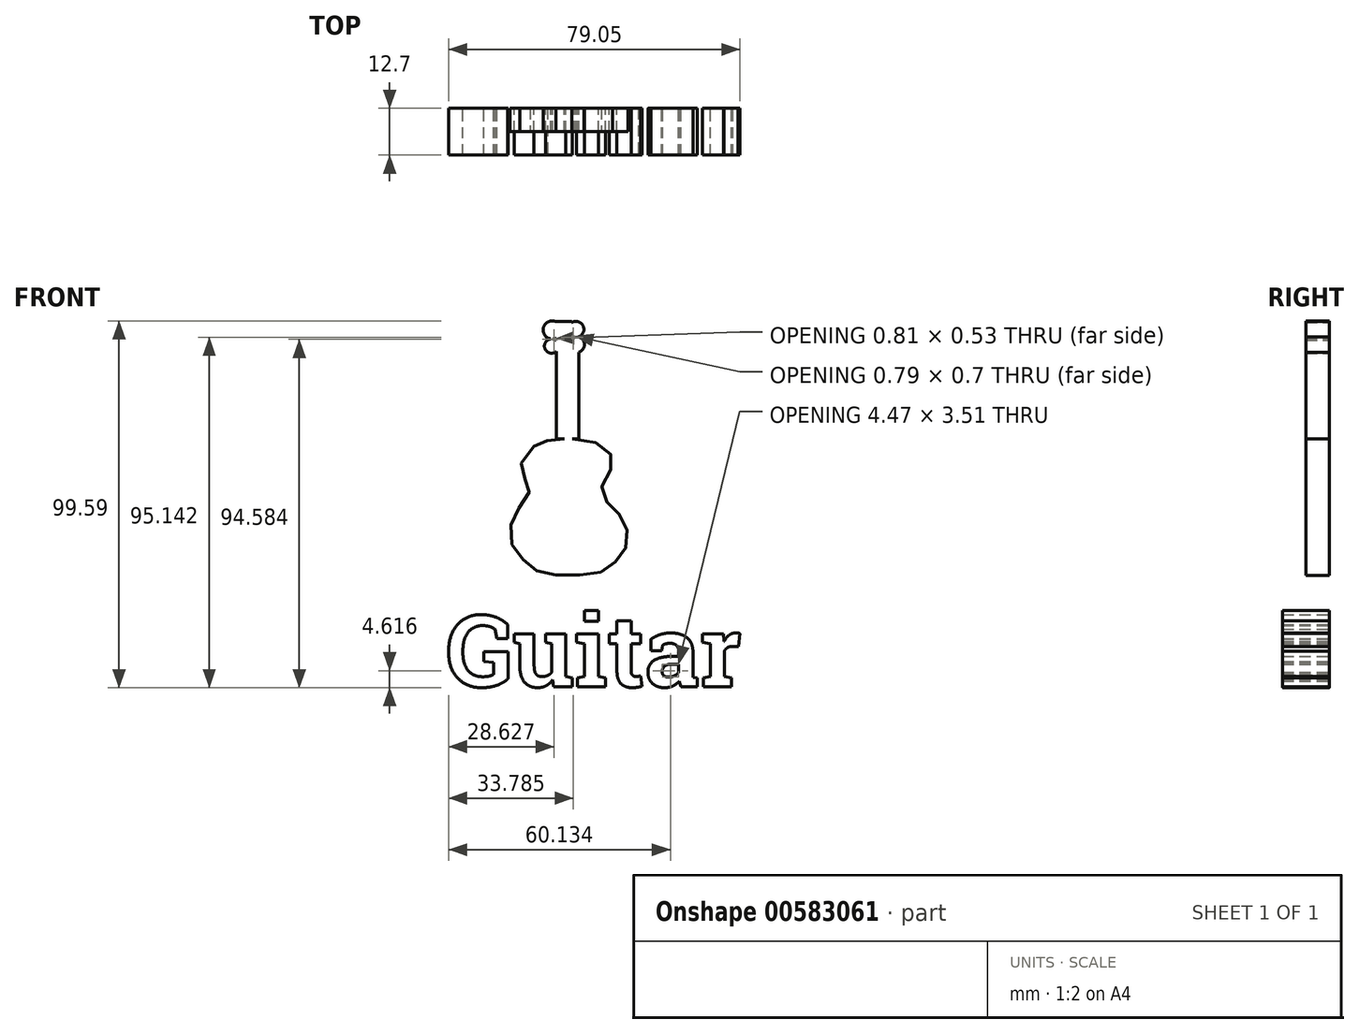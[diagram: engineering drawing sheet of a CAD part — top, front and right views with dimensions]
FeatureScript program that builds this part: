
annotation { "Feature Type Name" : "Feature", "Feature Type Description" : "" }
export const myFeature = defineFeature(function(context is Context, id is Id, definition is map)
    precondition{}
    {
        {
            var Q0;
            Q0=qCreatedBy(makeId("Front.planeOp"),FACE);
            var sketch = newSketch(context, id + "F0", { "sketchPlane" : qUnion([Q0])});
            skFitSpline(sketch, "E0", {"points": [v(-6.16, 9) * mm, v(-10.52, 8.25) * mm, v(-13.94, 6.35) * mm, v(-16.97, 0) * mm, v(-14.31, -3.5) * mm, v(-16.02, -8.06) * mm, v(-19.05, -12.99) * mm, v(-19.24, -19.62) * mm, v(-15.45, -24.36) * mm, v(-11.1, -27.4) * mm, v(-2.56, -27.97) * mm, v(5.4, -27.02) * mm, v(9.57, -23.6) * mm, v(12.23, -19.05) * mm, v(11.1, -13.18) * mm, v(8.06, -9.57) * mm, v(5.02, -5.21) * mm, v(7.3, 0) * mm, v(7.87, 4.27) * mm, v(3.32, 8.06) * mm, v(-6.16, 9) * mm]});
            skSolve(sketch);
        }
        {
            var Q0;
            Q0=makeQuery(id+"F0.imprint","IMPRINT",FACE,{"disambiguationData":[TD([[makeQuery(id+"F0.imprint","IMPRINT",EDGE,{"derivedFrom":sQuery(id+"F0.wireOp",EDGE,"E0")}),1.0]])]});
            extrude(context, id + "F1", {"entities" : qUnion([Q0]), "depth" : 6.35 * mm, "offsetDistance" : 25.4 * mm});
        }
        {
            var Q0;
            Q0=qCreatedBy(makeId("Front.planeOp"),FACE);
            var sketch = newSketch(context, id + "F2", { "sketchPlane" : qUnion([Q0])});
            skLineSegment(sketch, "E1.bottom", {"start": v(-7.17, 33.27) * mm, "end": v(-1, 33.27) * mm});
            skLineSegment(sketch, "E1.top", {"start": v(-7.17, 9.07) * mm, "end": v(-1, 9.07) * mm});
            skLineSegment(sketch, "E1.left", {"start": v(-7.17, 33.27) * mm, "end": v(-7.17, 9.07) * mm});
            skLineSegment(sketch, "E1.right", {"start": v(-1, 33.27) * mm, "end": v(-1, 9.07) * mm});
            skSolve(sketch);
        }
        {
            var Q0;
            Q0=makeQuery(id+"F2.imprint","IMPRINT",FACE,{"disambiguationData":[TD([[makeQuery(id+"F2.imprint","IMPRINT",EDGE,{"derivedFrom":sQuery(id+"F2.wireOp",EDGE,"E1.bottom")}),-1.0]])]});
            extrude(context, id + "F3", {"entities" : qUnion([Q0]), "operationType" : NewBodyOperationType.ADD, "depth" : 6.35 * mm, "offsetDistance" : 25.4 * mm});
        }
        {
            var Q0;
            Q0=qCreatedBy(makeId("Front.planeOp"),FACE);
            var sketch = newSketch(context, id + "F4", { "sketchPlane" : qUnion([Q0])});
            skCircle(sketch, "E2", {"center": v(-8.44, 34.22) * mm, "radius": 1.93 * mm});
            skSolve(sketch);
        }
        {
            var Q0;
            Q0 = qSketchRegion(id + "F4", true);
            extrude(context, id + "F5", {"entities" : qUnion([Q0]), "operationType" : NewBodyOperationType.ADD, "depth" : 6.35 * mm, "offsetDistance" : 25.4 * mm});
        }
        {
            var Q0;
            Q0=qCreatedBy(makeId("Front.planeOp"),FACE);
            var sketch = newSketch(context, id + "F6", { "sketchPlane" : qUnion([Q0])});
            skCircle(sketch, "E3", {"center": v(-1.61, 34.6) * mm, "radius": 2.12 * mm});
            skSolve(sketch);
        }
        {
            var Q0;
            Q0 = qSketchRegion(id + "F6", true);
            extrude(context, id + "F7", {"entities" : qUnion([Q0]), "operationType" : NewBodyOperationType.ADD, "depth" : 6.35 * mm, "offsetDistance" : 25.4 * mm});
        }
        {
            var Q0;
            Q0=qCreatedBy(makeId("Front.planeOp"),FACE);
            var sketch = newSketch(context, id + "F8", { "sketchPlane" : qUnion([Q0])});
            skCircle(sketch, "E4", {"center": v(-1.8, 38.77) * mm, "radius": 2.15 * mm});
            skSolve(sketch);
        }
        {
            var Q0;
            Q0 = qSketchRegion(id + "F8", true);
            extrude(context, id + "F9", {"entities" : qUnion([Q0]), "operationType" : NewBodyOperationType.ADD, "depth" : 6.35 * mm, "offsetDistance" : 25.4 * mm});
        }
        {
            var Q0;
            Q0=qCreatedBy(makeId("Front.planeOp"),FACE);
            var sketch = newSketch(context, id + "F10", { "sketchPlane" : qUnion([Q0])});
            skCircle(sketch, "E5", {"center": v(-8.25, 38.58) * mm, "radius": 2.46 * mm});
            skSolve(sketch);
        }
        {
            var Q0;
            Q0 = qSketchRegion(id + "F10", true);
            extrude(context, id + "F11", {"entities" : qUnion([Q0]), "operationType" : NewBodyOperationType.ADD, "depth" : 6.35 * mm, "offsetDistance" : 25.4 * mm});
        }
        {
            var Q0;
            Q0=qCreatedBy(makeId("Front.planeOp"),FACE);
            var sketch = newSketch(context, id + "F12", { "sketchPlane" : qUnion([Q0])});
            skLineSegment(sketch, "E6.bottom", {"start": v(-7.3, 40.86) * mm, "end": v(-2.94, 40.86) * mm});
            skLineSegment(sketch, "E6.top", {"start": v(-7.3, 32.9) * mm, "end": v(-2.94, 32.9) * mm});
            skLineSegment(sketch, "E6.left", {"start": v(-7.3, 40.86) * mm, "end": v(-7.3, 32.9) * mm});
            skLineSegment(sketch, "E6.right", {"start": v(-2.94, 40.86) * mm, "end": v(-2.94, 32.9) * mm});
            skSolve(sketch);
        }
        {
            var Q0;
            Q0 = qSketchRegion(id + "F12", true);
            extrude(context, id + "F13", {"entities" : qUnion([Q0]), "operationType" : NewBodyOperationType.ADD, "depth" : 6.35 * mm, "offsetDistance" : 25.4 * mm});
        }
        {
            var Q0;
            Q0=qCreatedBy(makeId("Front.planeOp"),FACE);
            var sketch = newSketch(context, id + "F14", { "sketchPlane" : qUnion([Q0])});
            skText(sketch, "E7", { "text": "Guitar\n", "fontName": "RobotoSlab-Bold.ttf"});
            const initialGuessF14  = {"E7": [-0.03695, -0.05826, 1, 0, 0.01952]};
            skSetInitialGuess(sketch, initialGuessF14);
            skSolve(sketch);
        }
        {
            var Q0;
            Q0 = qSketchRegion(id + "F14", true);
            extrude(context, id + "F15", {"entities" : qUnion([Q0]), "depth" : 12.7 * mm, "offsetDistance" : 25.4 * mm});
        }
    });
